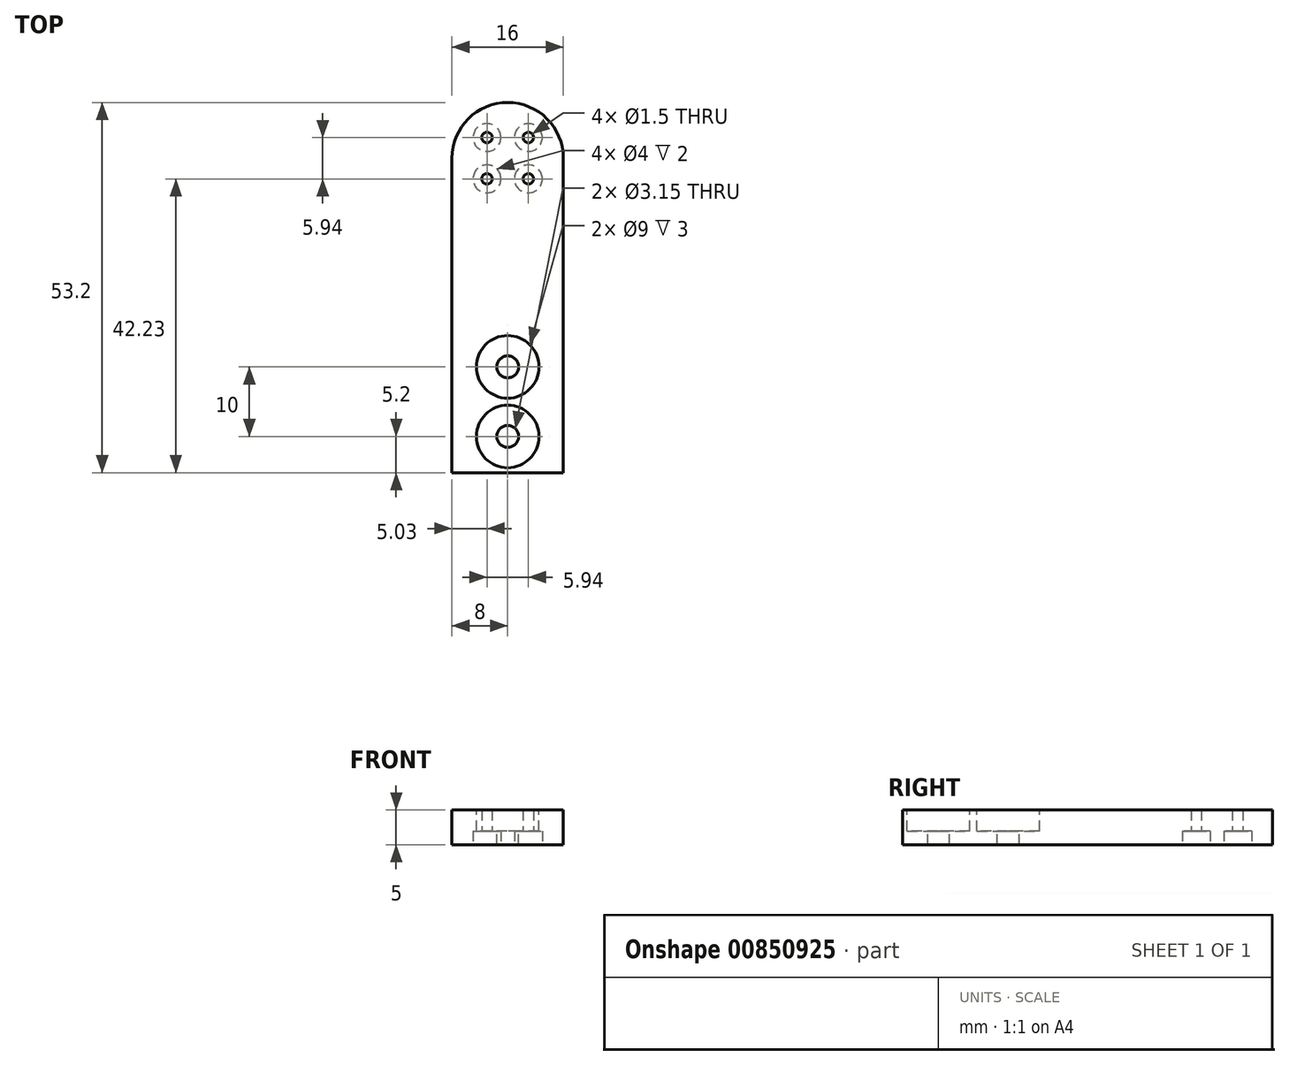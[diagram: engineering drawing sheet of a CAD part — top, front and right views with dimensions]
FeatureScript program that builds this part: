
annotation { "Feature Type Name" : "Feature", "Feature Type Description" : "" }
export const myFeature = defineFeature(function(context is Context, id is Id, definition is map)
    precondition{}
    {
        {
            var Q0;
            Q0=qCreatedBy(makeId("Top.planeOp"),FACE);
            var sketch = newSketch(context, id + "F0", { "sketchPlane" : qUnion([Q0])});
            skLineSegment(sketch, "E0", {"start": v(-8, 0) * mm, "end": v(-8, 35) * mm});
            skLineSegment(sketch, "E1", {"start": v(8, 0) * mm, "end": v(8, 35) * mm});
            skArc(sketch, "E2", {"start": v(-8, 35) * mm, "mid": v(0, 43) * mm, "end": v(8, 35) * mm});
            skLineSegment(sketch, "E3", {"start": v(-8, 0) * mm, "end": v(8, 0) * mm, "construction": true});
            skLineSegment(sketch, "E4", {"start": v(0, 35) * mm, "end": v(0, 24.43) * mm, "construction": true});
            skLineSegment(sketch, "E5", {"start": v(0, 24.43) * mm, "end": v(0, 35) * mm, "construction": true});
            skLineSegment(sketch, "E6", {"start": v(0, 35) * mm, "end": v(20.9, 35) * mm, "construction": true});
            skLineSegment(sketch, "E7.MirrorCS", {"start": v(8, 0) * mm, "end": v(8, -35) * mm});
            skLineSegment(sketch, "E8.MirrorCS", {"start": v(-8, 0) * mm, "end": v(-8, -35) * mm});
            skArc(sketch, "E9.MirrorCS", {"start": v(-8, -35) * mm, "mid": v(0, -43) * mm, "end": v(8, -35) * mm});
            skLineSegment(sketch, "E10.MirrorCS", {"start": v(0, -35) * mm, "end": v(20.9, -35) * mm, "construction": true});
            skLineSegment(sketch, "E11.MirrorCS", {"start": v(0, -24.43) * mm, "end": v(0, -35) * mm, "construction": true});
            skCircle(sketch, "E12", {"center": v(0, 35) * mm, "radius": 4.2 * mm, "construction": true});
            skCircle(sketch, "E13", {"center": v(2.97, 37.97) * mm, "radius": 0.75 * mm});
            skLineSegment(sketch, "E14", {"start": v(0, 35) * mm, "end": v(2.97, 37.97) * mm, "construction": true});
            skCircle(sketch, "E15.MirrorC", {"center": v(2.97, 32.03) * mm, "radius": 0.75 * mm});
            skCircle(sketch, "E16.MirrorC", {"center": v(-2.97, 32.03) * mm, "radius": 0.75 * mm});
            skCircle(sketch, "E17.MirrorC", {"center": v(-2.97, 37.97) * mm, "radius": 0.75 * mm});
            skCircle(sketch, "E18.MirrorC", {"center": v(-2.97, -32.03) * mm, "radius": 0.75 * mm});
            skCircle(sketch, "E19.MirrorC", {"center": v(2.97, -32.03) * mm, "radius": 0.75 * mm});
            skCircle(sketch, "E20.MirrorC", {"center": v(-2.97, -37.97) * mm, "radius": 0.75 * mm});
            skCircle(sketch, "E21.MirrorC", {"center": v(2.97, -37.97) * mm, "radius": 0.75 * mm});
            skCircle(sketch, "E22.MirrorC", {"center": v(0, -35) * mm, "radius": 4.2 * mm, "construction": true});
            skSolve(sketch);
        }
        {
            var Q0;
            Q0=qSketchRegion(id+"F0",true);
            extrude(context, id + "F1", {"entities" : qUnion([Q0]), "depth" : 5 * mm, "offsetDistance" : 25 * mm});
        }
        {
            var Q0;
            Q0=makeQuery(id+"F1.opExtrude","CAP_FACE",FACE,{"disambiguationData":[OSD([sQuery(id+"F0.wireOp",EDGE,"E0"),sQuery(id+"F0.wireOp",EDGE,"E1"),sQuery(id+"F0.wireOp",EDGE,"E2"),sQuery(id+"F0.wireOp",EDGE,"E7.MirrorCS"),sQuery(id+"F0.wireOp",EDGE,"E8.MirrorCS"),sQuery(id+"F0.wireOp",EDGE,"E9.MirrorCS"),sQuery(id+"F0.wireOp",EDGE,"E13"),sQuery(id+"F0.wireOp",EDGE,"E15.MirrorC"),sQuery(id+"F0.wireOp",EDGE,"E16.MirrorC"),sQuery(id+"F0.wireOp",EDGE,"E17.MirrorC"),sQuery(id+"F0.wireOp",EDGE,"E18.MirrorC"),sQuery(id+"F0.wireOp",EDGE,"E19.MirrorC"),sQuery(id+"F0.wireOp",EDGE,"E20.MirrorC"),sQuery(id+"F0.wireOp",EDGE,"E21.MirrorC")])],"isStart":false});
            var sketch = newSketch(context, id + "F2", { "sketchPlane" : qUnion([Q0])});
            skCircle(sketch, "E23", {"center": v(0, 5) * mm, "radius": 1.57 * mm});
            skLineSegment(sketch, "E24", {"start": v(0, 0) * mm, "end": v(0, 8.86) * mm, "construction": true});
            skLineSegment(sketch, "E25", {"start": v(0, 8.86) * mm, "end": v(0, 0) * mm, "construction": true});
            skLineSegment(sketch, "E26", {"start": v(5.05, 0) * mm, "end": v(0, 0) * mm, "construction": true});
            skCircle(sketch, "E27.MirrorC", {"center": v(0, -5) * mm, "radius": 1.57 * mm});
            skSolve(sketch);
        }
        {
            var Q0;
            Q0=qSketchRegion(id+"F2",true);
            extrude(context, id + "F3", {"entities" : qUnion([Q0]), "operationType" : NewBodyOperationType.REMOVE, "endBound" : BoundingType.THROUGH_ALL, "oppositeDirection" : true, "depth" : 25 * mm, "offsetDistance" : 25 * mm});
        }
        {
            var Q0;
            Q0=makeQuery(id+"F1.opExtrude","CAP_FACE",FACE,{"disambiguationData":[OSD([sQuery(id+"F0.wireOp",EDGE,"E0"),sQuery(id+"F0.wireOp",EDGE,"E1"),sQuery(id+"F0.wireOp",EDGE,"E2"),sQuery(id+"F0.wireOp",EDGE,"E7.MirrorCS"),sQuery(id+"F0.wireOp",EDGE,"E8.MirrorCS"),sQuery(id+"F0.wireOp",EDGE,"E9.MirrorCS"),sQuery(id+"F0.wireOp",EDGE,"E13"),sQuery(id+"F0.wireOp",EDGE,"E15.MirrorC"),sQuery(id+"F0.wireOp",EDGE,"E16.MirrorC"),sQuery(id+"F0.wireOp",EDGE,"E17.MirrorC"),sQuery(id+"F0.wireOp",EDGE,"E18.MirrorC"),sQuery(id+"F0.wireOp",EDGE,"E19.MirrorC"),sQuery(id+"F0.wireOp",EDGE,"E20.MirrorC"),sQuery(id+"F0.wireOp",EDGE,"E21.MirrorC")])],"isStart":false});
            var sketch = newSketch(context, id + "F4", { "sketchPlane" : qUnion([Q0])});
            skCircle(sketch, "E28", {"center": v(0, 5) * mm, "radius": 4.5 * mm});
            skCircle(sketch, "E29", {"center": v(0, -5) * mm, "radius": 4.5 * mm});
            skSolve(sketch);
        }
        {
            var Q0;
            Q0=qSketchRegion(id+"F4",true);
            extrude(context, id + "F5", {"entities" : qUnion([Q0]), "operationType" : NewBodyOperationType.REMOVE, "oppositeDirection" : true, "depth" : 3 * mm, "offsetDistance" : 25 * mm});
        }
        {
            var Q0;
            Q0=makeQuery(id+"F1.opExtrude","CAP_FACE",FACE,{"disambiguationData":[OSD([sQuery(id+"F0.wireOp",EDGE,"E0"),sQuery(id+"F0.wireOp",EDGE,"E1"),sQuery(id+"F0.wireOp",EDGE,"E2"),sQuery(id+"F0.wireOp",EDGE,"E7.MirrorCS"),sQuery(id+"F0.wireOp",EDGE,"E8.MirrorCS"),sQuery(id+"F0.wireOp",EDGE,"E9.MirrorCS"),sQuery(id+"F0.wireOp",EDGE,"E13"),sQuery(id+"F0.wireOp",EDGE,"E15.MirrorC"),sQuery(id+"F0.wireOp",EDGE,"E16.MirrorC"),sQuery(id+"F0.wireOp",EDGE,"E17.MirrorC"),sQuery(id+"F0.wireOp",EDGE,"E18.MirrorC"),sQuery(id+"F0.wireOp",EDGE,"E19.MirrorC"),sQuery(id+"F0.wireOp",EDGE,"E20.MirrorC"),sQuery(id+"F0.wireOp",EDGE,"E21.MirrorC")])],"isStart":true});
            var sketch = newSketch(context, id + "F6", { "sketchPlane" : qUnion([Q0])});
            skCircle(sketch, "E30", {"center": v(-2.97, 37.97) * mm, "radius": 2 * mm});
            skLineSegment(sketch, "E31", {"start": v(0, 0) * mm, "end": v(0, 35) * mm, "construction": true});
            skLineSegment(sketch, "E32", {"start": v(0, 35) * mm, "end": v(13.56, 35) * mm, "construction": true});
            skCircle(sketch, "E33.MirrorC", {"center": v(2.97, 37.97) * mm, "radius": 2 * mm});
            skCircle(sketch, "E34.MirrorC", {"center": v(2.97, 32.03) * mm, "radius": 2 * mm});
            skCircle(sketch, "E35.MirrorC", {"center": v(-2.97, 32.03) * mm, "radius": 2 * mm});
            skLineSegment(sketch, "E36", {"start": v(0, 0) * mm, "end": v(13.4, 0) * mm, "construction": true});
            skCircle(sketch, "E37.MirrorC", {"center": v(-2.97, -32.03) * mm, "radius": 2 * mm});
            skCircle(sketch, "E38.MirrorC", {"center": v(-2.97, -37.97) * mm, "radius": 2 * mm});
            skCircle(sketch, "E39.MirrorC", {"center": v(2.97, -37.97) * mm, "radius": 2 * mm});
            skCircle(sketch, "E40.MirrorC", {"center": v(2.97, -32.03) * mm, "radius": 2 * mm});
            skSolve(sketch);
        }
        {
            var Q0;
            Q0=qSketchRegion(id+"F6",true);
            extrude(context, id + "F7", {"entities" : qUnion([Q0]), "operationType" : NewBodyOperationType.REMOVE, "oppositeDirection" : true, "depth" : 2 * mm, "offsetDistance" : 25 * mm});
        }
        {
            var Q0;
            Q0=makeQuery(id+"F1.opExtrude","SWEPT_FACE",FACE,{"disambiguationData":[OSD([sQuery(id+"F0.wireOp",EDGE,"E1"),sQuery(id+"F0.wireOp",EDGE,"E7.MirrorCS")])]});
            var sketch = newSketch(context, id + "F8", { "sketchPlane" : qUnion([Q0])});
            skLineSegment(sketch, "E41.bottom", {"start": v(-10.2, 0) * mm, "end": v(-53.3, 0) * mm});
            skLineSegment(sketch, "E41.top", {"start": v(-10.2, 7.9) * mm, "end": v(-53.3, 7.9) * mm});
            skLineSegment(sketch, "E41.left", {"start": v(-10.2, 0) * mm, "end": v(-10.2, 7.9) * mm});
            skLineSegment(sketch, "E41.right", {"start": v(-53.3, 0) * mm, "end": v(-53.3, 7.9) * mm});
            skSolve(sketch);
        }
        {
            var Q0;
            Q0 = qSketchRegion(id + "F8", true);
            extrude(context, id + "F9", {"entities" : qUnion([Q0]), "operationType" : NewBodyOperationType.REMOVE, "endBound" : BoundingType.THROUGH_ALL, "oppositeDirection" : true, "depth" : 25 * mm, "offsetDistance" : 25 * mm});
        }
    });
